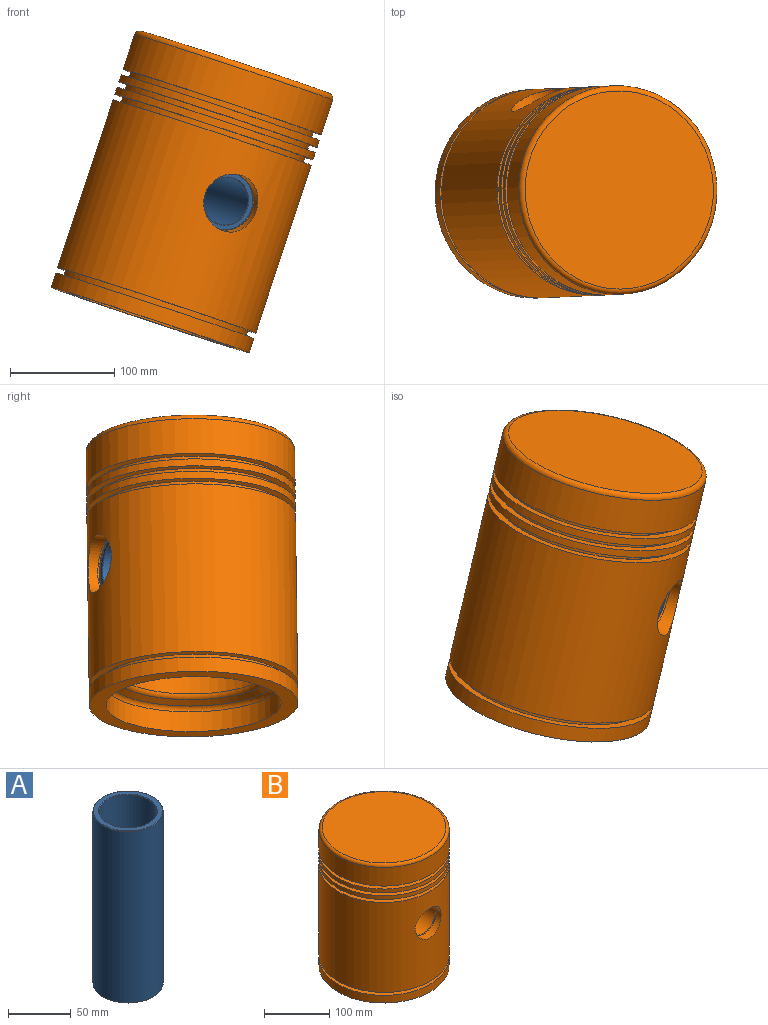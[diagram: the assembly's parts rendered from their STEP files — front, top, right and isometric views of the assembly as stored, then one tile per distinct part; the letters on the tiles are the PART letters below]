
ASSEMBLY  parts=2 mates=1
PART A: 8 faces, bbox 56x56x168 mm
  f0: cylinder r=23mm len=167.2mm, axis (0,0,-1), area 24162.6mm2, adj f4,f7
  f1: cylinder r=28mm len=167.2mm, axis (0,0,-1), area 29415.4mm2, adj f5,f6
  f2: plane 55.2x55.2mm, normal (0,0,1), area 672.9mm2, adj f6,f7
  f3: plane 55.2x55.2mm, normal (0,0,-1), area 672.9mm2, adj f4,f5
  f4: cone r=23.4mm half-angle=45deg, axis (0,0,-1), area 82.5mm2, adj f0,f3
  f5: cone r=28mm half-angle=45deg, axis (0,0,1), area 98.8mm2, adj f1,f3
  f6: cone r=27.6mm half-angle=45deg, axis (0,0,-1), area 98.8mm2, adj f1,f2
  f7: cone r=23mm half-angle=45deg, axis (0,0,1), area 82.5mm2, adj f0,f2
PART B: 53 faces, bbox 216.5x216.5x260 mm
  f0: cylinder r=100mm len=200mm, axis (0,0,1), area 101330.5mm2, adj f8,f9,f45,f49
  f1: cylinder r=72.5mm len=145mm, axis (0,0,1), area 42646mm2, adj f21,f22,f43,f44
  f2: plane 200x200mm, normal (0,0,1), area 4767.6mm2, adj f3,f36
  f3: cylinder r=100mm len=200mm, axis (0,0,1), area 4398.2mm2, adj f2,f4
  f4: plane 200x200mm, normal (0,0,-1), area 4767.6mm2, adj f3,f5
  f5: torus R=92.1mm, axis (0,0,1), area 90.8mm2, adj f4,f6
  f6: cylinder r=92mm len=184mm, axis (0,0,1), area 3121.5mm2, adj f5,f7
  f7: torus R=92.1mm, axis (0,0,1), area 90.8mm2, adj f6,f8
  f8: plane 200x200mm, normal (0,0,1), area 4767.6mm2, adj f0,f7
  f9: plane 200x200mm, normal (0,0,-1), area 4825.5mm2, adj f0,f10
  f10: cylinder r=92mm len=184mm, axis (0,0,1), area 3237.1mm2, adj f9,f11
  f11: plane 200x200mm, normal (0,0,1), area 4825.5mm2, adj f10,f12
  f12: cylinder r=100mm len=200mm, axis (0,0,1), area 9047.8mm2, adj f11,f13
  f13: plane 200x200mm, normal (0,0,-1), area 9248.8mm2, adj f12,f14
  f14: cylinder r=84mm len=168mm, axis (0,0,1), area 10555.8mm2, adj f13,f15
  f15: torus R=78mm, axis (0,0,1), area 3041.8mm2, adj f14,f16
  f16: cone r=81.39mm half-angle=55.6deg, axis (0,0,-1), area 3737.1mm2, adj f15,f17
  f17: torus R=78.5mm, axis (0,0,1), area 2686.7mm2, adj f16,f18
  f18: cylinder r=72.5mm len=145mm, axis (0,0,1), area 9476.9mm2, adj f17,f19
  f19: plane 155x155mm, normal (0,0,1), area 2356.2mm2, adj f18,f20
  f20: cylinder r=77.5mm len=155mm, axis (0,0,1), area 9738.9mm2, adj f19,f21
  f21: plane 155x155mm, normal (0,0,-1), area 2356.2mm2, adj f1,f20
  f22: torus R=37.5mm, axis (0,0,1), area 20650.8mm2, adj f1,f23
  f23: plane 75x75mm, normal (0,0,-1), area 4417.9mm2, adj f22
  f24: plane 190x190mm, normal (0,0,1), area 28352.9mm2, adj f25
  f25: torus R=95mm, axis (0,0,1), area 4845.1mm2, adj f24,f26
  f26: cylinder r=100mm len=200mm, axis (0,0,1), area 21991.1mm2, adj f25,f27
  f27: plane 200x200mm, normal (0,0,-1), area 4767.6mm2, adj f26,f28
  f28: torus R=92.1mm, axis (0,0,1), area 90.8mm2, adj f27,f29
  f29: cylinder r=92mm len=184mm, axis (0,0,1), area 3121.5mm2, adj f28,f30
  f30: torus R=92.1mm, axis (0,0,1), area 90.8mm2, adj f29,f31
  f31: plane 200x200mm, normal (0,0,1), area 4767.6mm2, adj f30,f32
  f32: cylinder r=100mm len=200mm, axis (0,0,1), area 4398.2mm2, adj f31,f33
  f33: plane 200x200mm, normal (0,0,-1), area 4767.6mm2, adj f32,f34
  f34: torus R=92.1mm, axis (0,0,1), area 90.8mm2, adj f33,f35
  f35: cylinder r=92mm len=184mm, axis (0,0,1), area 3121.5mm2, adj f34,f36
  f36: torus R=92.1mm, axis (0,0,1), area 90.8mm2, adj f2,f35
  f37: cone r=42.5mm half-angle=5.8deg, axis (0,1,0), area 5271.2mm2, adj f38,f44
  f38: plane 75x75mm, normal (0,-1,0), area 1954.9mm2, adj f37,f39
  f39: cylinder r=28mm len=56mm, axis (0,-1,0), area 8013.1mm2, adj f38,f48
  f40: cylinder r=28mm len=56mm, axis (0,-1,0), area 8013.1mm2, adj f41,f52
  f41: plane 75x75mm, normal (0,1,0), area 1954.9mm2, adj f40,f42
  f42: cone r=42.5mm half-angle=5.8deg, axis (0,-1,0), area 5271mm2, adj f41,f43
  f43: bspline ~94.17x90.94mm, area 2488mm2, adj f1,f42
  f44: bspline ~94.16x90.94mm, area 2490.3mm2, adj f1,f37
  f45: cylinder r=28mm len=56mm, axis (0,-1,0), area 2086.8mm2, adj f0,f47
  f46: cylinder r=29.5mm len=59mm, axis (0,-1,0), area 398.5mm2, adj f47,f48
  f47: plane 59x59mm, normal (0,-1,0), area 271mm2, adj f45,f46
  f48: plane 59x59mm, normal (0,1,0), area 271mm2, adj f39,f46
  f49: cylinder r=28mm len=56mm, axis (0,1,0), area 2086mm2, adj f0,f51
  f50: cylinder r=29.5mm len=59mm, axis (0,1,0), area 398.5mm2, adj f51,f52
  f51: plane 59x59mm, normal (0,1,0), area 271mm2, adj f49,f50
  f52: plane 59x59mm, normal (0,-1,0), area 271mm2, adj f40,f50
PLACE A rot(axis=(0.94,0.34,0.04),96.6deg) t=(98.3,-218.69,195.75)mm
PLACE B rot(axis=(0.1,0.61,0.78),29.6deg) t=(129.97,-295.48,186.3)mm
MATE revolute B.f46 <-> A.f0  axis (0.38,-0.92,-0.11) through (161.79,-372.64,176.8)mm
